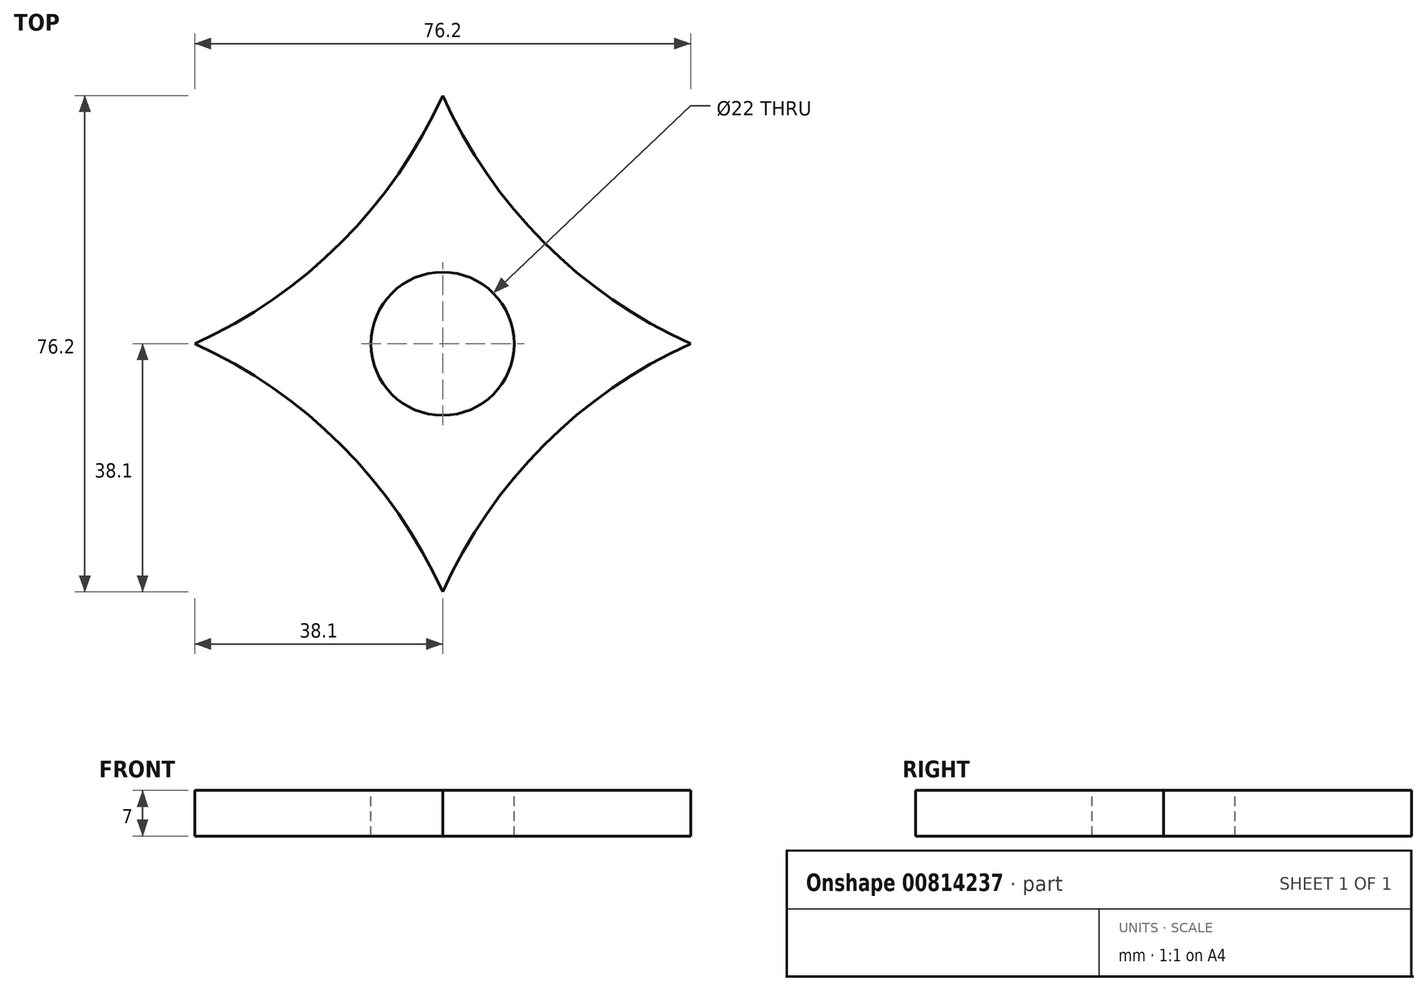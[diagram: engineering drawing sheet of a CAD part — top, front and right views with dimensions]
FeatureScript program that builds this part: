
annotation { "Feature Type Name" : "Feature", "Feature Type Description" : "" }
export const myFeature = defineFeature(function(context is Context, id is Id, definition is map)
    precondition{}
    {
        {
            var Q0;
            Q0=qCreatedBy(makeId("Top.planeOp"),FACE);
            var sketch = newSketch(context, id + "F0", { "sketchPlane" : qUnion([Q0])});
            skCircle(sketch, "E0", {"center": v(0, 0) * mm, "radius": 38.1 * mm});
            skArc(sketch, "E1", {"start": v(38.1, 0) * mm, "mid": v(15.57, -15.57) * mm, "end": v(0, -38.1) * mm});
            skArc(sketch, "E2", {"start": v(0, 38.1) * mm, "mid": v(15.57, 15.57) * mm, "end": v(38.1, 0) * mm});
            skArc(sketch, "E3", {"start": v(-38.1, 0) * mm, "mid": v(-15.57, 15.57) * mm, "end": v(0, 38.1) * mm});
            skArc(sketch, "E4", {"start": v(0, -38.1) * mm, "mid": v(-15.57, -15.57) * mm, "end": v(-38.1, 0) * mm});
            skSolve(sketch);
        }
        {
            var Q0;
            Q0=makeQuery(id+"F0.imprint","IMPRINT",FACE,{"disambiguationData":[TD([[makeQuery(id+"F0.imprint","IMPRINT",EDGE,{"derivedFrom":sQuery(id+"F0.wireOp",EDGE,"E1")}),-1.0]])]});
            extrude(context, id + "F1", {"entities" : qUnion([Q0]), "depth" : 7 * mm, "offsetDistance" : 25.4 * mm});
        }
        {
            var Q0;
            Q0=makeQuery(id+"F1.opExtrude","CAP_FACE",FACE,{"disambiguationData":[OSD([sQuery(id+"F0.wireOp",EDGE,"E1"),sQuery(id+"F0.wireOp",EDGE,"E2"),sQuery(id+"F0.wireOp",EDGE,"E3"),sQuery(id+"F0.wireOp",EDGE,"E4")])],"isStart":false});
            var sketch = newSketch(context, id + "F2", { "sketchPlane" : qUnion([Q0])});
            skCircle(sketch, "E5", {"center": v(0, 0) * mm, "radius": 11 * mm});
            skSolve(sketch);
        }
        {
            var Q0;
            Q0=makeQuery(id+"F2.imprint","IMPRINT",FACE,{"disambiguationData":[TD([[makeQuery(id+"F2.imprint","IMPRINT",EDGE,{"derivedFrom":sQuery(id+"F2.wireOp",EDGE,"E5")}),1.0]])]});
            extrude(context, id + "F3", {"entities" : qUnion([Q0]), "operationType" : NewBodyOperationType.REMOVE, "endBound" : BoundingType.THROUGH_ALL, "oppositeDirection" : true, "depth" : 25.4 * mm, "offsetDistance" : 25.4 * mm});
        }
    });
